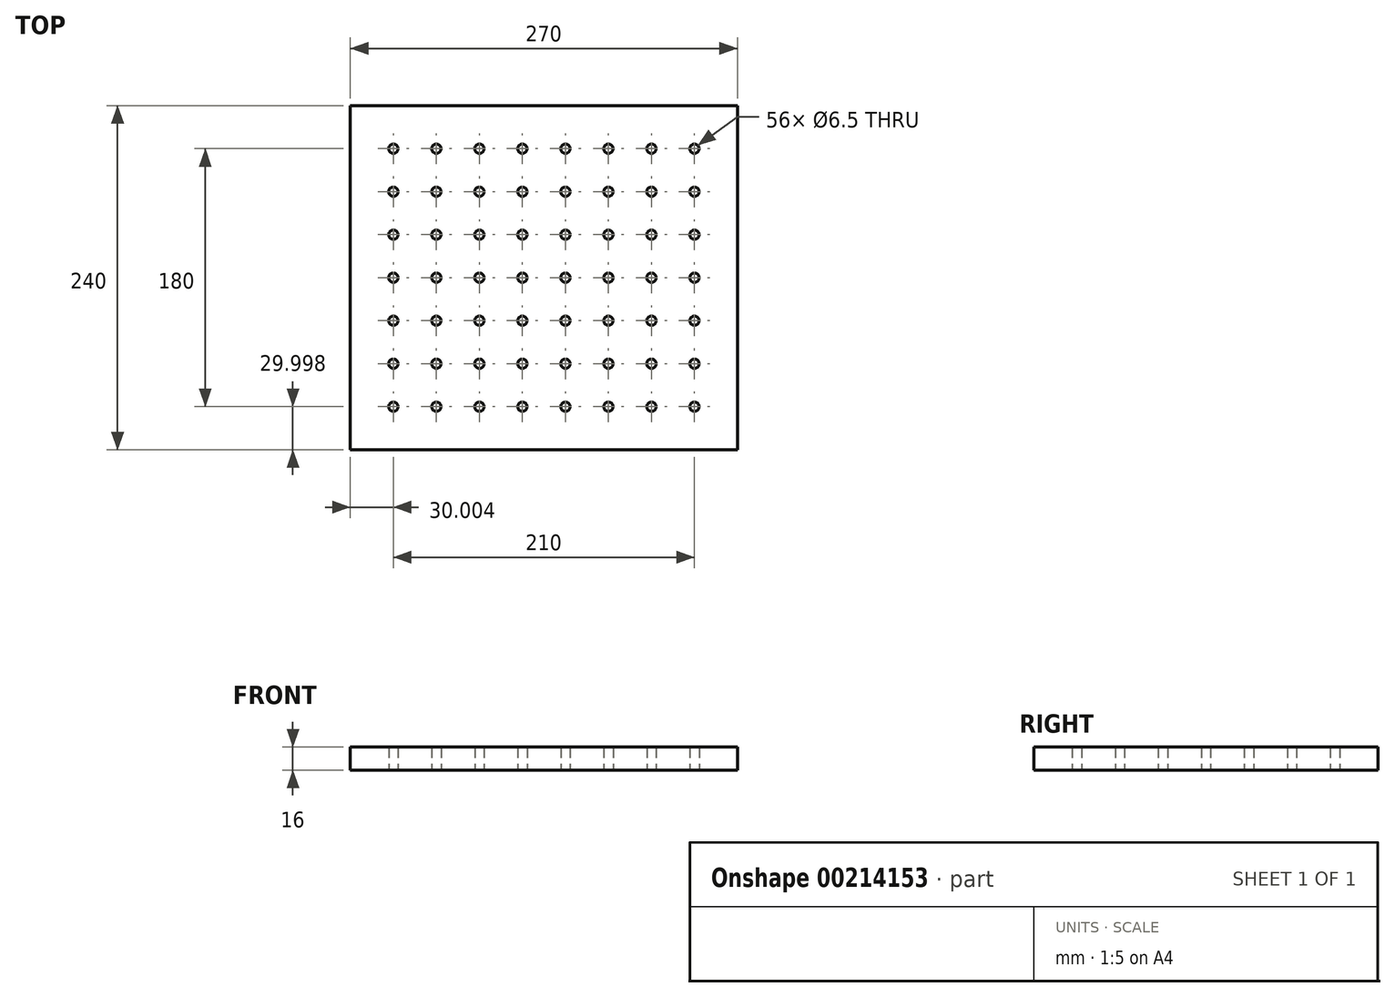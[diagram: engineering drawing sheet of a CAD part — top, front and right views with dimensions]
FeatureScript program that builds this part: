
annotation { "Feature Type Name" : "Feature", "Feature Type Description" : "" }
export const myFeature = defineFeature(function(context is Context, id is Id, definition is map)
    precondition{}
    {
        {
            var Q0;
            Q0=qCreatedBy(makeId("Top.planeOp"),FACE);
            var sketch = newSketch(context, id + "F0", { "sketchPlane" : qUnion([Q0])});
            skLineSegment(sketch, "E0.bottom", {"start": v(-39.32, 202.55) * mm, "end": v(230.68, 202.55) * mm});
            skLineSegment(sketch, "E0.top", {"start": v(-39.32, -37.45) * mm, "end": v(230.68, -37.45) * mm});
            skLineSegment(sketch, "E0.left", {"start": v(-39.32, 202.55) * mm, "end": v(-39.32, -37.45) * mm});
            skLineSegment(sketch, "E0.right", {"start": v(230.68, 202.55) * mm, "end": v(230.68, -37.45) * mm});
            skCircle(sketch, "E1", {"center": v(-9.32, 172.55) * mm, "radius": 3.25 * mm});
            skCircle(sketch, "E2.1.0.0", {"center": v(20.68, 172.55) * mm, "radius": 3.25 * mm});
            skCircle(sketch, "E2.2.0.0", {"center": v(50.68, 172.55) * mm, "radius": 3.25 * mm});
            skCircle(sketch, "E2.3.0.0", {"center": v(80.68, 172.55) * mm, "radius": 3.25 * mm});
            skCircle(sketch, "E2.4.0.0", {"center": v(110.68, 172.55) * mm, "radius": 3.25 * mm});
            skCircle(sketch, "E2.5.0.0", {"center": v(140.68, 172.55) * mm, "radius": 3.25 * mm});
            skCircle(sketch, "E2.6.0.0", {"center": v(170.68, 172.55) * mm, "radius": 3.25 * mm});
            skCircle(sketch, "E2.7.0.0", {"center": v(200.68, 172.55) * mm, "radius": 3.25 * mm});
            skLineSegment(sketch, "E2.direction1", {"start": v(-9.32, 172.55) * mm, "end": v(20.68, 172.55) * mm, "construction": true});
            skCircle(sketch, "E3.1.0.0", {"center": v(200.68, 142.55) * mm, "radius": 3.25 * mm});
            skCircle(sketch, "E3.2.0.0", {"center": v(200.68, 112.55) * mm, "radius": 3.25 * mm});
            skLineSegment(sketch, "E3.direction1", {"start": v(200.68, 172.55) * mm, "end": v(200.68, 142.55) * mm, "construction": true});
            skCircle(sketch, "E4.0.3.0", {"center": v(200.68, 82.55) * mm, "radius": 3.25 * mm});
            skCircle(sketch, "E4.0.4.0", {"center": v(200.68, 52.55) * mm, "radius": 3.25 * mm});
            skCircle(sketch, "E4.0.5.0", {"center": v(200.68, 22.55) * mm, "radius": 3.25 * mm});
            skCircle(sketch, "E4.0.6.0", {"center": v(200.68, -7.45) * mm, "radius": 3.25 * mm});
            skCircle(sketch, "E5.1.0.0", {"center": v(170.68, 142.55) * mm, "radius": 3.25 * mm});
            skCircle(sketch, "E5.2.0.0", {"center": v(140.68, 142.55) * mm, "radius": 3.25 * mm});
            skCircle(sketch, "E5.3.0.0", {"center": v(110.68, 142.55) * mm, "radius": 3.25 * mm});
            skCircle(sketch, "E5.4.0.0", {"center": v(80.68, 142.55) * mm, "radius": 3.25 * mm});
            skCircle(sketch, "E5.5.0.0", {"center": v(50.68, 142.55) * mm, "radius": 3.25 * mm});
            skCircle(sketch, "E5.6.0.0", {"center": v(20.68, 142.55) * mm, "radius": 3.25 * mm});
            skCircle(sketch, "E5.7.0.0", {"center": v(-9.32, 142.55) * mm, "radius": 3.25 * mm});
            skLineSegment(sketch, "E5.direction1", {"start": v(200.68, 142.55) * mm, "end": v(170.68, 142.55) * mm, "construction": true});
            skCircle(sketch, "E6.1.0.0", {"center": v(170.68, 112.55) * mm, "radius": 3.25 * mm});
            skCircle(sketch, "E6.2.0.0", {"center": v(140.68, 112.55) * mm, "radius": 3.25 * mm});
            skCircle(sketch, "E6.3.0.0", {"center": v(110.68, 112.55) * mm, "radius": 3.25 * mm});
            skCircle(sketch, "E6.4.0.0", {"center": v(80.68, 112.55) * mm, "radius": 3.25 * mm});
            skCircle(sketch, "E6.5.0.0", {"center": v(50.68, 112.55) * mm, "radius": 3.25 * mm});
            skCircle(sketch, "E6.6.0.0", {"center": v(20.68, 112.55) * mm, "radius": 3.25 * mm});
            skCircle(sketch, "E6.7.0.0", {"center": v(-9.32, 112.55) * mm, "radius": 3.25 * mm});
            skLineSegment(sketch, "E6.direction1", {"start": v(200.68, 112.55) * mm, "end": v(170.68, 112.55) * mm, "construction": true});
            skCircle(sketch, "E7.1.0.0", {"center": v(170.68, 82.55) * mm, "radius": 3.25 * mm});
            skCircle(sketch, "E7.2.0.0", {"center": v(140.68, 82.55) * mm, "radius": 3.25 * mm});
            skCircle(sketch, "E7.3.0.0", {"center": v(110.68, 82.55) * mm, "radius": 3.25 * mm});
            skCircle(sketch, "E7.4.0.0", {"center": v(80.68, 82.55) * mm, "radius": 3.25 * mm});
            skCircle(sketch, "E7.5.0.0", {"center": v(50.68, 82.55) * mm, "radius": 3.25 * mm});
            skCircle(sketch, "E7.6.0.0", {"center": v(20.68, 82.55) * mm, "radius": 3.25 * mm});
            skCircle(sketch, "E7.7.0.0", {"center": v(-9.32, 82.55) * mm, "radius": 3.25 * mm});
            skLineSegment(sketch, "E7.direction1", {"start": v(200.68, 82.55) * mm, "end": v(170.68, 82.55) * mm, "construction": true});
            skCircle(sketch, "E8.1.0.0", {"center": v(170.68, 52.55) * mm, "radius": 3.25 * mm});
            skCircle(sketch, "E8.2.0.0", {"center": v(140.68, 52.55) * mm, "radius": 3.25 * mm});
            skCircle(sketch, "E8.3.0.0", {"center": v(110.68, 52.55) * mm, "radius": 3.25 * mm});
            skCircle(sketch, "E8.4.0.0", {"center": v(80.68, 52.55) * mm, "radius": 3.25 * mm});
            skCircle(sketch, "E8.5.0.0", {"center": v(50.68, 52.55) * mm, "radius": 3.25 * mm});
            skCircle(sketch, "E8.6.0.0", {"center": v(20.68, 52.55) * mm, "radius": 3.25 * mm});
            skCircle(sketch, "E8.7.0.0", {"center": v(-9.32, 52.55) * mm, "radius": 3.25 * mm});
            skLineSegment(sketch, "E8.direction1", {"start": v(200.68, 52.55) * mm, "end": v(170.68, 52.55) * mm, "construction": true});
            skCircle(sketch, "E9.1.0.0", {"center": v(170.68, 22.55) * mm, "radius": 3.25 * mm});
            skCircle(sketch, "E9.2.0.0", {"center": v(140.68, 22.55) * mm, "radius": 3.25 * mm});
            skCircle(sketch, "E9.3.0.0", {"center": v(110.68, 22.55) * mm, "radius": 3.25 * mm});
            skCircle(sketch, "E9.4.0.0", {"center": v(80.68, 22.55) * mm, "radius": 3.25 * mm});
            skCircle(sketch, "E9.5.0.0", {"center": v(50.68, 22.55) * mm, "radius": 3.25 * mm});
            skCircle(sketch, "E9.6.0.0", {"center": v(20.68, 22.55) * mm, "radius": 3.25 * mm});
            skCircle(sketch, "E9.7.0.0", {"center": v(-9.32, 22.55) * mm, "radius": 3.25 * mm});
            skLineSegment(sketch, "E9.direction1", {"start": v(200.68, 22.55) * mm, "end": v(170.68, 22.55) * mm, "construction": true});
            skCircle(sketch, "E10.1.0.0", {"center": v(170.68, -7.45) * mm, "radius": 3.25 * mm});
            skCircle(sketch, "E10.2.0.0", {"center": v(140.68, -7.45) * mm, "radius": 3.25 * mm});
            skCircle(sketch, "E10.3.0.0", {"center": v(110.68, -7.45) * mm, "radius": 3.25 * mm});
            skCircle(sketch, "E10.4.0.0", {"center": v(80.68, -7.45) * mm, "radius": 3.25 * mm});
            skCircle(sketch, "E10.5.0.0", {"center": v(50.68, -7.45) * mm, "radius": 3.25 * mm});
            skCircle(sketch, "E10.6.0.0", {"center": v(20.68, -7.45) * mm, "radius": 3.25 * mm});
            skCircle(sketch, "E10.7.0.0", {"center": v(-9.32, -7.45) * mm, "radius": 3.25 * mm});
            skLineSegment(sketch, "E10.direction1", {"start": v(200.68, -7.45) * mm, "end": v(170.68, -7.45) * mm, "construction": true});
            skSolve(sketch);
        }
        {
            var Q0;
            Q0=makeQuery(id+"F0.imprint","IMPRINT",FACE,{"disambiguationData":[TD([[makeQuery(id+"F0.imprint","IMPRINT",EDGE,{"derivedFrom":sQuery(id+"F0.wireOp",EDGE,"E0.bottom")}),-1.0]])]});
            extrude(context, id + "F1", {"entities" : qUnion([Q0]), "depth" : 16 * mm});
        }
    });
